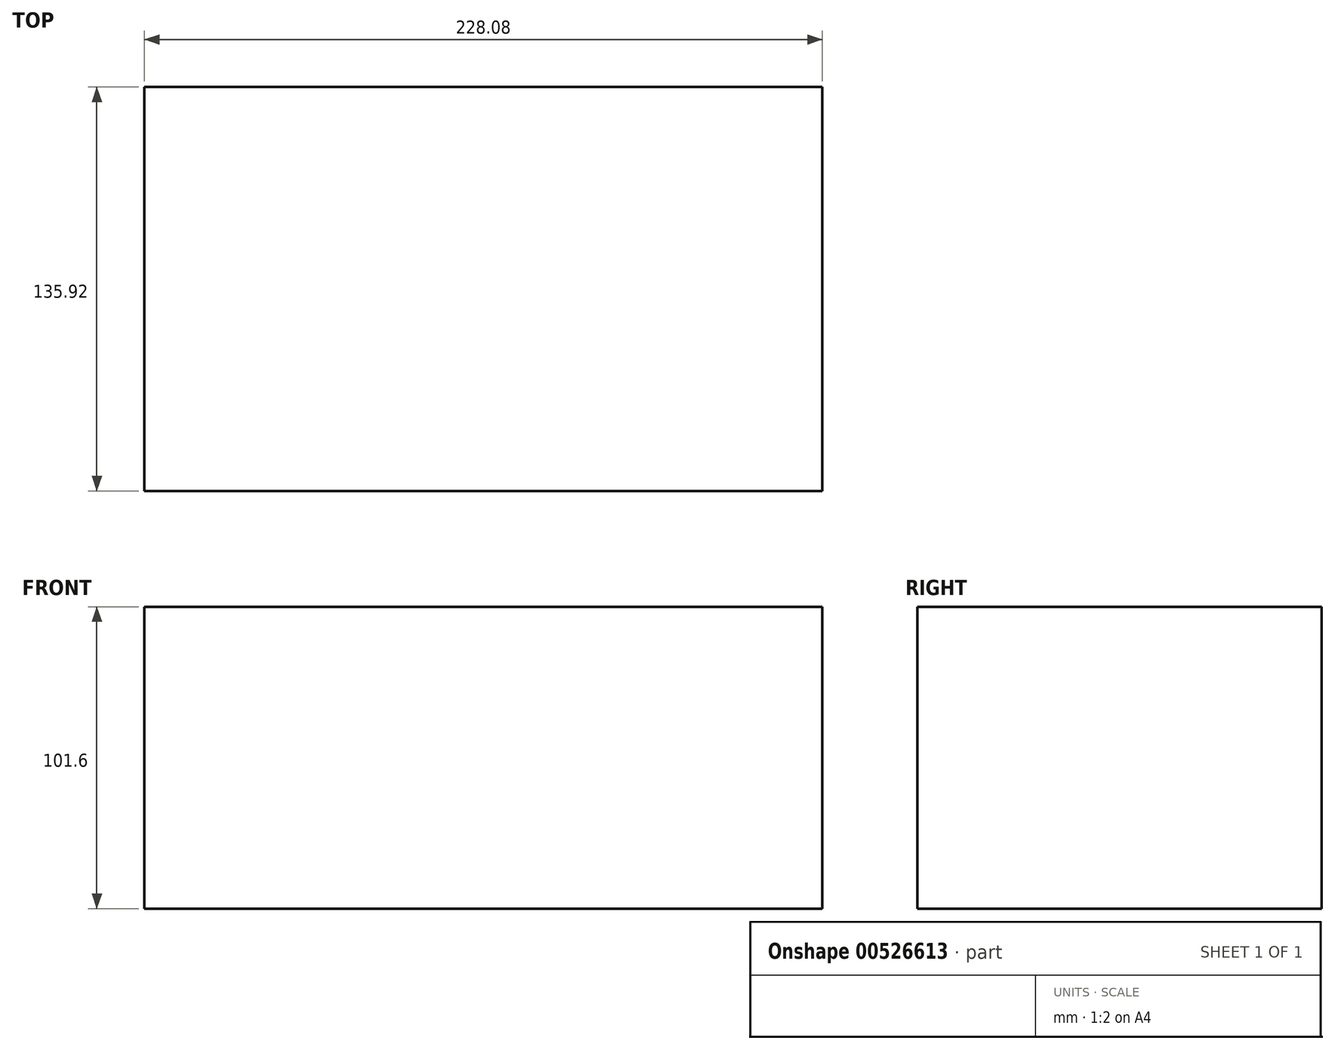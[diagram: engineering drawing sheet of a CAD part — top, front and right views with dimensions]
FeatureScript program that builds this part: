
annotation { "Feature Type Name" : "Feature", "Feature Type Description" : "" }
export const myFeature = defineFeature(function(context is Context, id is Id, definition is map)
    precondition{}
    {
        {
            var Q0;
            Q0=qCreatedBy(makeId("Top.planeOp"),FACE);
            var sketch = newSketch(context, id + "F0", { "sketchPlane" : qUnion([Q0])});
            skLineSegment(sketch, "E0.bottom", {"start": v(-102.62, 56.49) * mm, "end": v(125.46, 56.49) * mm});
            skLineSegment(sketch, "E0.top", {"start": v(-102.62, -79.43) * mm, "end": v(125.46, -79.43) * mm});
            skLineSegment(sketch, "E0.left", {"start": v(-102.62, 56.49) * mm, "end": v(-102.62, -79.43) * mm});
            skLineSegment(sketch, "E0.right", {"start": v(125.46, 56.49) * mm, "end": v(125.46, -79.43) * mm});
            skSolve(sketch);
        }
        {
            var Q0;
            Q0 = qSketchRegion(id + "F0", true);
            extrude(context, id + "F1", {"entities" : qUnion([Q0]), "depth" : 101.6 * mm, "offsetDistance" : 25.4 * mm});
        }
    });
